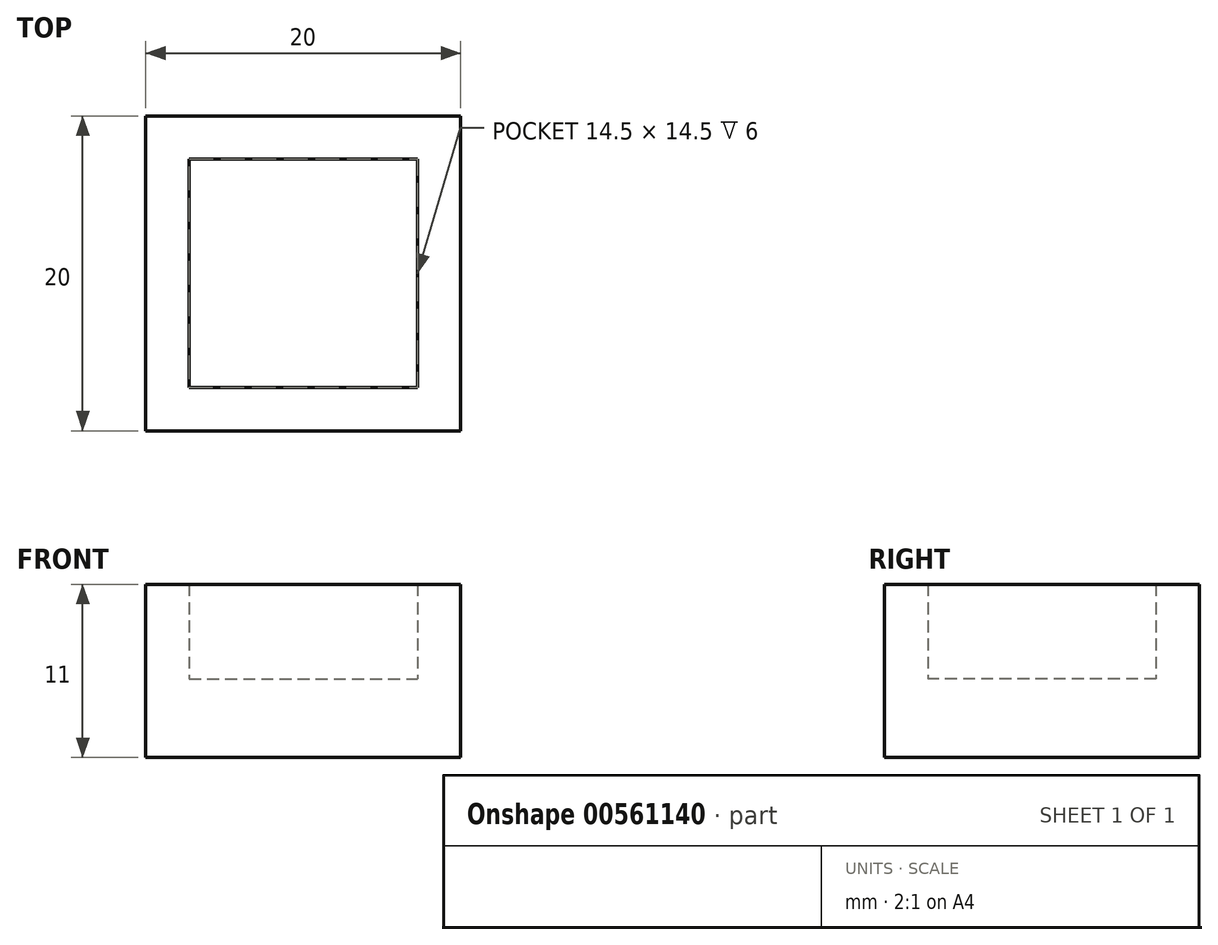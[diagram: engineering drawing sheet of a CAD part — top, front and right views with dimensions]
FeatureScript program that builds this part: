
annotation { "Feature Type Name" : "Feature", "Feature Type Description" : "" }
export const myFeature = defineFeature(function(context is Context, id is Id, definition is map)
    precondition{}
    {
        {
            assignVariable(context, id + "F0", {"name" : "wall_width", "anyValue" : 5});
        }
        {
            assignVariable(context, id + "F1", {"name" : "height", "anyValue" : 6});
        }
        {
            var Q0;
            Q0=qCreatedBy(makeId("Top.planeOp"),FACE);
            var sketch = newSketch(context, id + "F2", { "sketchPlane" : qUnion([Q0])});
            skLineSegment(sketch, "E0.bottom", {"start": v(0, 0) * mm, "end": v(20, 0) * mm});
            skLineSegment(sketch, "E0.top", {"start": v(0, -20) * mm, "end": v(20, -20) * mm});
            skLineSegment(sketch, "E0.left", {"start": v(0, 0) * mm, "end": v(0, -20) * mm});
            skLineSegment(sketch, "E0.right", {"start": v(20, 0) * mm, "end": v(20, -20) * mm});
            skSolve(sketch);
        }
        {
            var Q0;
            Q0 = qSketchRegion(id + "F2", true);
            extrude(context, id + "F3", {"entities" : qUnion([Q0]), "depth" : (getVariable(context, 'wall_width')) * mm, "offsetDistance" : 25 * mm});
        }
        {
            var Q0;
            Q0=makeQuery(id+"F3.opExtrude","CAP_FACE",FACE,{"disambiguationData":[OSD([sQuery(id+"F2.wireOp",EDGE,"E0.bottom"),sQuery(id+"F2.wireOp",EDGE,"E0.top"),sQuery(id+"F2.wireOp",EDGE,"E0.left"),sQuery(id+"F2.wireOp",EDGE,"E0.right")])],"isStart":false});
            var sketch = newSketch(context, id + "F4", { "sketchPlane" : qUnion([Q0])});
            skLineSegment(sketch, "E1.bottom", {"start": v(2.75, -2.75) * mm, "end": v(17.25, -2.75) * mm});
            skLineSegment(sketch, "E1.top", {"start": v(2.75, -17.25) * mm, "end": v(17.25, -17.25) * mm});
            skLineSegment(sketch, "E1.left", {"start": v(2.75, -2.75) * mm, "end": v(2.75, -17.25) * mm});
            skLineSegment(sketch, "E1.right", {"start": v(17.25, -2.75) * mm, "end": v(17.25, -17.25) * mm});
            skLineSegment(sketch, "E2", {"start": v(2.75, -2.75) * mm, "end": v(0, -2.75) * mm, "construction": true});
            skLineSegment(sketch, "E3", {"start": v(2.75, -17.25) * mm, "end": v(2.75, -20) * mm, "construction": true});
            skLineSegment(sketch, "E4", {"start": v(17.25, -17.25) * mm, "end": v(20, -17.25) * mm, "construction": true});
            skLineSegment(sketch, "E5", {"start": v(17.25, -2.75) * mm, "end": v(17.25, 0) * mm, "construction": true});
            skSolve(sketch);
        }
        {
            var Q0;
            Q0=makeQuery(id+"F4.imprint","IMPRINT",FACE,{"disambiguationData":[TD([[makeQuery(id+"F4.imprint","IMPRINT",EDGE,{"derivedFrom":sQuery(id+"F4.wireOp",EDGE,"E1.bottom")}),1.0]])]});
            extrude(context, id + "F5", {"entities" : qUnion([Q0]), "operationType" : NewBodyOperationType.ADD, "depth" : (getVariable(context, 'height')) * mm, "offsetDistance" : 25 * mm});
        }
    });
